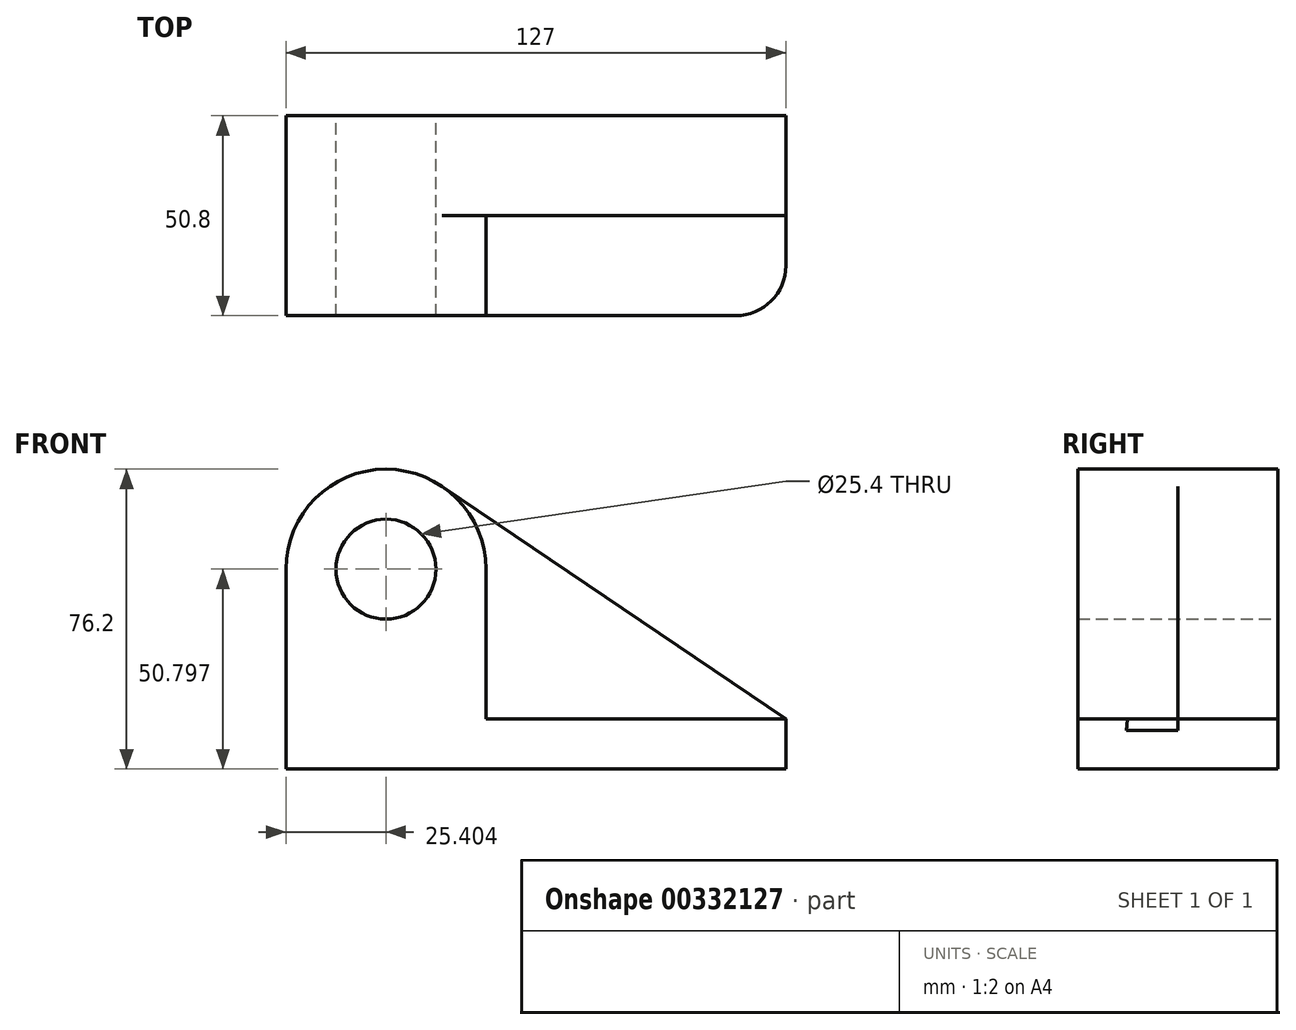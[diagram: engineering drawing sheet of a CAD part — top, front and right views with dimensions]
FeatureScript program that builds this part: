
annotation { "Feature Type Name" : "Feature", "Feature Type Description" : "" }
export const myFeature = defineFeature(function(context is Context, id is Id, definition is map)
    precondition{}
    {
        {
            var Q0;
            Q0=qCreatedBy(makeId("Front.planeOp"),FACE);
            var sketch = newSketch(context, id + "F0", { "sketchPlane" : qUnion([Q0])});
            skCircle(sketch, "E0", {"center": v(-49.8, 40.92) * mm, "radius": 12.7 * mm});
            skArc(sketch, "E1", {"start": v(-35.56, 61.95) * mm, "mid": v(-61.7, 63.35) * mm, "end": v(-75.2, 40.92) * mm});
            skLineSegment(sketch, "E2", {"start": v(-75.2, 40.92) * mm, "end": v(-75.2, -9.88) * mm});
            skLineSegment(sketch, "E3", {"start": v(-75.2, -9.88) * mm, "end": v(51.8, -9.88) * mm});
            skLineSegment(sketch, "E4", {"start": v(51.8, -9.88) * mm, "end": v(51.8, 2.82) * mm});
            skLineSegment(sketch, "E5", {"start": v(51.8, 2.82) * mm, "end": v(-35.56, 61.95) * mm});
            skSolve(sketch);
        }
        {
            var Q0;
            Q0 = qSketchRegion(id + "F0", true);
            extrude(context, id + "F1", {"entities" : qUnion([Q0]), "depth" : 25.4 * mm});
        }
        {
            var Q0;
            Q0=makeQuery(id+"F1.opExtrude","CAP_FACE",FACE,{"disambiguationData":[OSD([sQuery(id+"F0.wireOp",EDGE,"E0"),sQuery(id+"F0.wireOp",EDGE,"E1"),sQuery(id+"F0.wireOp",EDGE,"E2"),sQuery(id+"F0.wireOp",EDGE,"E3"),sQuery(id+"F0.wireOp",EDGE,"E4"),sQuery(id+"F0.wireOp",EDGE,"E5")])],"isStart":false});
            var sketch = newSketch(context, id + "F2", { "sketchPlane" : qUnion([Q0])});
            skCircle(sketch, "E6", {"center": v(-49.8, 40.92) * mm, "radius": 12.7 * mm});
            skArc(sketch, "E7", {"start": v(-24.4, 40.92) * mm, "mid": v(-49.8, 66.32) * mm, "end": v(-75.2, 40.92) * mm});
            skLineSegment(sketch, "E8", {"start": v(-75.2, 40.92) * mm, "end": v(-75.2, 0) * mm});
            skPoint(sketch, "E8.endSnap0", {"position": v(-75.2, 15.52) * mm});
            skLineSegment(sketch, "E9", {"start": v(-24.4, 40.92) * mm, "end": v(-24.4, 2.82) * mm});
            skLineSegment(sketch, "E10.bottom", {"start": v(51.8, 0) * mm, "end": v(51.8, 0) * mm});
            skLineSegment(sketch, "E10.top", {"start": v(-75.2, -9.88) * mm, "end": v(51.8, -9.88) * mm});
            skLineSegment(sketch, "E10.left", {"start": v(-75.2, 0) * mm, "end": v(-75.2, -9.88) * mm});
            skLineSegment(sketch, "E10.right", {"start": v(51.8, 0) * mm, "end": v(51.8, -0.37) * mm});
            skLineSegment(sketch, "E11", {"start": v(51.8, 2.82) * mm, "end": v(-24.4, 2.82) * mm});
            skLineSegment(sketch, "E12", {"start": v(51.78, -9.8) * mm, "end": v(51.8, 2.82) * mm});
            skSolve(sketch);
        }
        {
            var Q0;
            Q0=makeQuery(id+"F2.imprint","IMPRINT",FACE,{"disambiguationData":[TD([[makeQuery(id+"F2.imprint","IMPRINT",EDGE,{"derivedFrom":sQuery(id+"F2.wireOp",EDGE,"E6")}),-1.0]])]});
            extrude(context, id + "F3", {"entities" : qUnion([Q0]), "operationType" : NewBodyOperationType.ADD, "depth" : 25.4 * mm});
        }
        {
            var Q0;
            Q0=makeQuery(id+"F3.opExtrude","CAP_EDGE",EDGE,{"disambiguationData":[OSD([sQuery(id+"F2.wireOp",EDGE,"E10.right")])],"isStart":false});
            fillet(context, id + "F4", {"entities" : qUnion([Q0]), "radius" : 12.7 * mm, "tangentPropagation" : true, "allowEdgeOverflow" : false});
        }
    });
